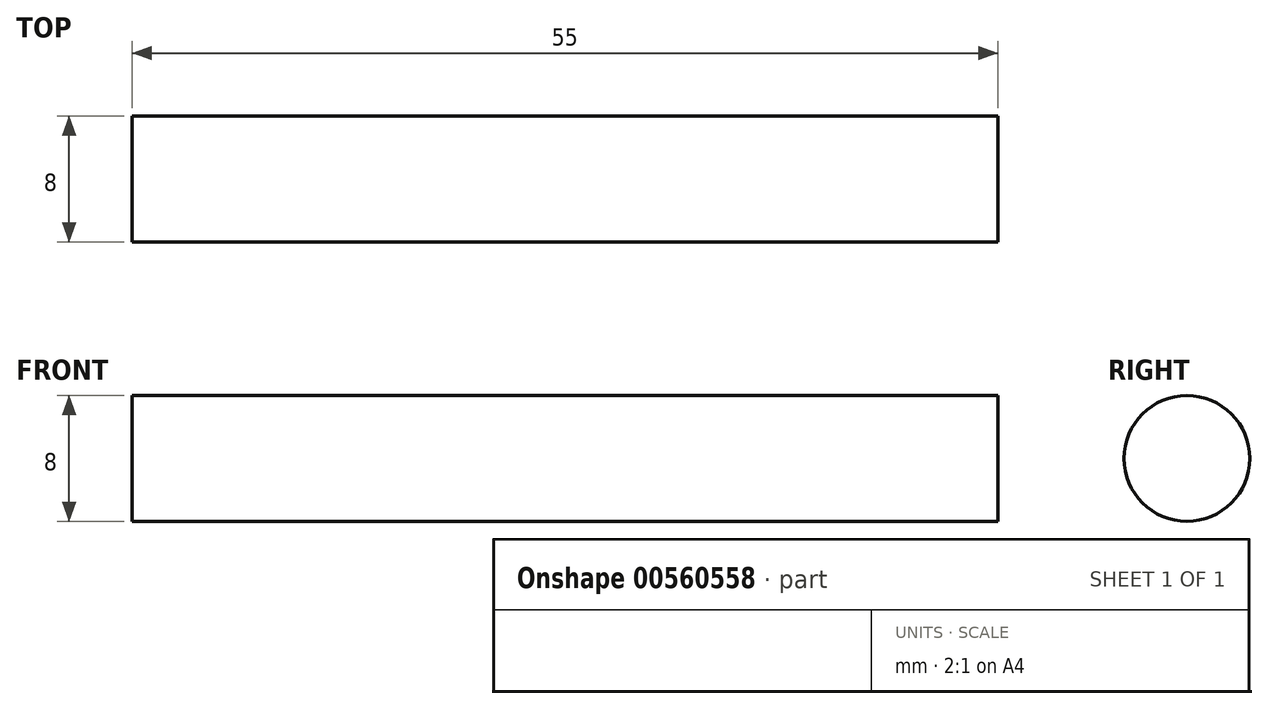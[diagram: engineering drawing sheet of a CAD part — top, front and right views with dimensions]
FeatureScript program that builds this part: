
annotation { "Feature Type Name" : "Feature", "Feature Type Description" : "" }
export const myFeature = defineFeature(function(context is Context, id is Id, definition is map)
    precondition{}
    {
        {
            var Q0;
            Q0=qCreatedBy(makeId("Right.planeOp"),FACE);
            var sketch = newSketch(context, id + "F0", { "sketchPlane" : qUnion([Q0])});
            skCircle(sketch, "E0", {"center": v(0, 0) * mm, "radius": 4 * mm});
            skSolve(sketch);
        }
        {
            var Q0;
            Q0=makeQuery(id+"F0.imprint","IMPRINT",FACE,{"disambiguationData":[TD([[makeQuery(id+"F0.imprint","IMPRINT",EDGE,{"derivedFrom":sQuery(id+"F0.wireOp",EDGE,"E0")}),1.0]])]});
            extrude(context, id + "F1", {"entities" : qUnion([Q0]), "depth" : 55 * mm, "offsetDistance" : 25 * mm});
        }
    });
